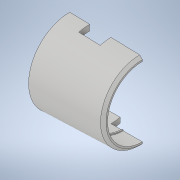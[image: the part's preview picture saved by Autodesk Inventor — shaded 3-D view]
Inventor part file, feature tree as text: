
AUTODESK INVENTOR PART (.ipt)
format: ipt  version: 2020.2 (Build 242310000, 310)  size: 159,744 bytes
history: native  units: mm
features: sketch x3, extrude x2, revolve x1, chamfer x1
ambient origin geometry x8: Origin, YZ Plane, XZ Plane, XY Plane, X Axis, Y Axis, Z Axis, Center Point
bodies: Solid1 (feature_tree)
feature tree (7):
  revolve  "Revolution1"  [1 undecoded]
  extrude  "Extrusion1"  Depth=200.0mm TaperAngle=0.0deg
  extrude  "Extrusion2"  Depth=11.85mm
  chamfer  "Chamfer1"  Distance=6.0mm
  sketch  "Sketch2"  dims[d2=40.25mm d3=9.7mm]
  sketch  "Sketch3"  dims[d9=270.0deg d17=200.0mm d18=0.0mm]
  sketch  "Sketch4"  dims[d21=11.0mm d23=5.0mm d24=6.0mm d25=11.0mm d27=200.0mm d28=0.0mm d31=1.5mm d32=2.0mm d33=45.0deg d34=0.5mm d36=0.7mm d41=19.3mm d43=11.85mm d44=11.85mm d45=11.35mm d46=22.85mm d47=21.675mm]
note: 1 required parameter value undecoded (feature->parameter linkage not recoverable at this tier; creation-order binding heuristic only, values carry confidence <= 0.55)
